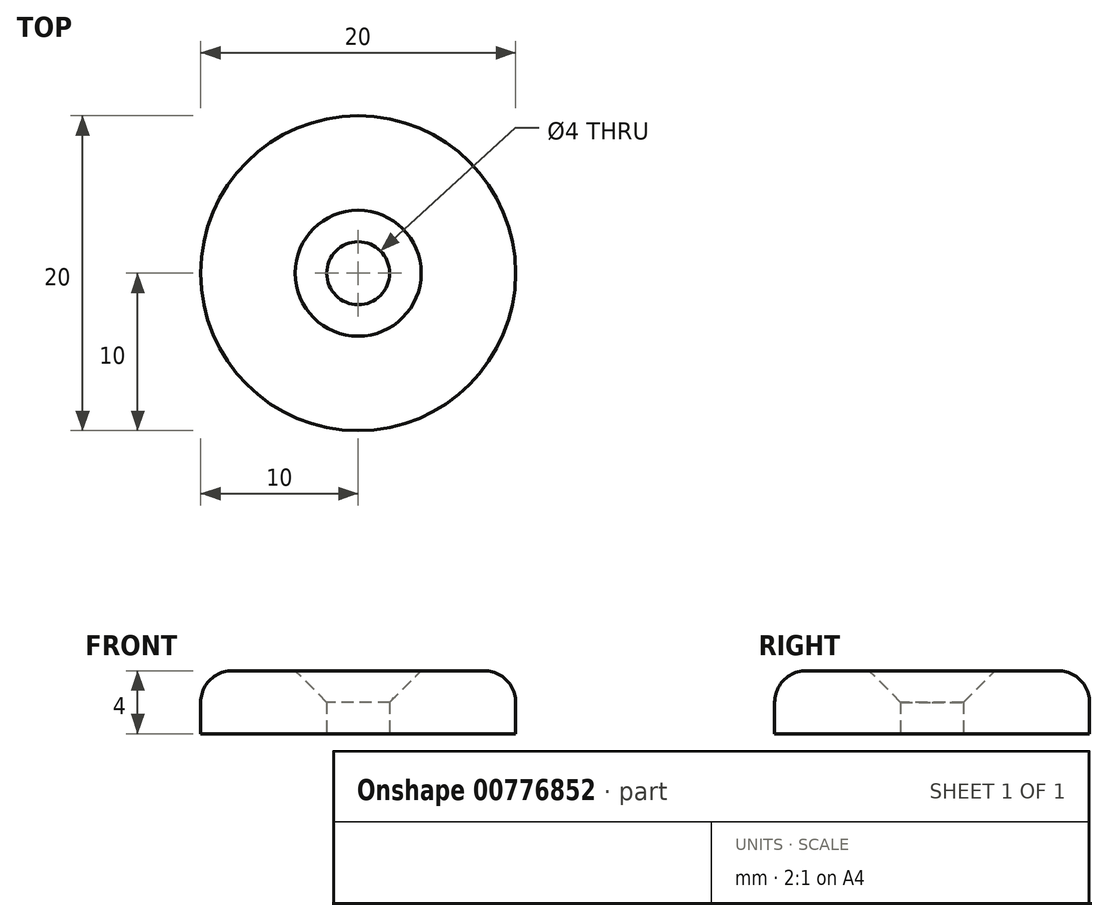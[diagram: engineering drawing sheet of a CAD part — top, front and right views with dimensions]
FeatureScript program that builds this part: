
annotation { "Feature Type Name" : "Feature", "Feature Type Description" : "" }
export const myFeature = defineFeature(function(context is Context, id is Id, definition is map)
    precondition{}
    {
        {
            var Q0;
            Q0=qCreatedBy(makeId("Top.planeOp"),FACE);
            var sketch = newSketch(context, id + "F0", { "sketchPlane" : qUnion([Q0])});
            skCircle(sketch, "E0", {"center": v(0, 0) * mm, "radius": 10 * mm});
            skCircle(sketch, "E1", {"center": v(0, 0) * mm, "radius": 2 * mm});
            skSolve(sketch);
        }
        {
            var Q0;
            Q0=makeQuery(id+"F0.imprint","IMPRINT",FACE,{"disambiguationData":[TD([[makeQuery(id+"F0.imprint","IMPRINT",EDGE,{"derivedFrom":sQuery(id+"F0.wireOp",EDGE,"E0")}),1.0]])]});
            extrude(context, id + "F1", {"entities" : qUnion([Q0]), "depth" : 4 * mm, "offsetDistance" : 25 * mm});
        }
        {
            var Q0;
            Q0=makeQuery(id+"F1.opExtrude","CAP_EDGE",EDGE,{"disambiguationData":[OSD([sQuery(id+"F0.wireOp",EDGE,"E0")])],"isStart":false});
            fillet(context, id + "F2", {"entities" : qUnion([Q0]), "radius" : 2 * mm, "tangentPropagation" : true, "allowEdgeOverflow" : false});
        }
        {
            var Q0;
            Q0=makeQuery(id+"F1.opExtrude","CAP_EDGE",EDGE,{"disambiguationData":[OSD([sQuery(id+"F0.wireOp",EDGE,"E1")])],"isStart":false});
            chamfer(context, id + "F3", {"entities" : qUnion([Q0]), "width" : 2 * mm, "tangentPropagation" : true});
        }
    });
